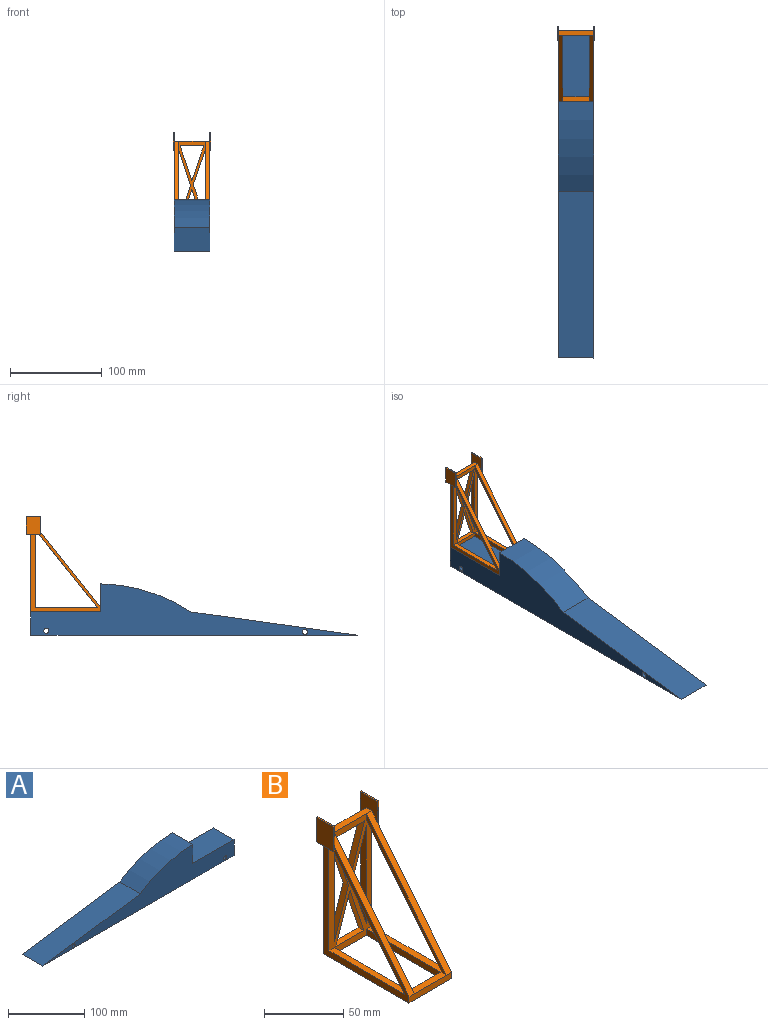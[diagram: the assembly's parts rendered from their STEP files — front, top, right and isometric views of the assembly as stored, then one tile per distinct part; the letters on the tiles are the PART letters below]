
ASSEMBLY  parts=2 mates=1
PART A: 10 faces, bbox 355.6x38.1x55.9 mm
  f0: plane 38.1x25.4mm, normal (1,0,0), area 967.7mm2, adj f1,f5,f6,f7
  f1: plane 76.2x38.1mm, normal (0,0,1), area 2903.2mm2, adj f0,f2,f6,f7
  f2: plane 38.1x30.48mm, normal (1,0,0), area 1161.3mm2, adj f1,f3,f6,f7
  f3: cylinder r=183.28mm len=97.84mm, axis (0,1,0), area 3957mm2, adj f2,f4,f6,f7
  f4: plane 181.56x38.1mm, normal (-0.14,0,0.99), area 6984.9mm2, adj f3,f5,f6,f7
  f5: plane 355.6x38.1mm, normal (0,0,-1), area 13548.4mm2, adj f0,f4,f6,f7
  f6: plane 355.6x55.88mm, normal (0,-1,0), area 8669.6mm2, adj f0,f1,f2,f3,f4,f5,f8,f9
  f7: plane 355.6x55.88mm, normal (0,1,0), area 8669.6mm2, adj f0,f1,f2,f3,f4,f5,f8,f9
  f8: cylinder r=2.79mm len=38.1mm, axis (0,-1,0), area 668.9mm2, adj f6,f7
  f9: cylinder r=2.79mm len=38.1mm, axis (0,-1,0), area 668.9mm2, adj f6,f7
PART B: 43 faces, bbox 40.6x81.4x103.5 mm
  f0: plane 66.68x4.76mm, normal (-1,0,0), area 317.5mm2, adj f3,f8,f20,f42
  f1: plane 66.68x4.76mm, normal (1,0,0), area 317.5mm2, adj f3,f8,f20,f42
  f2: plane 87.44x76.2mm, normal (-1,0,0), area 1049.8mm2, adj f3,f8,f11,f20,f22,f26,f27,f29
  f3: plane 93.98x38.1mm, normal (0,-1,0), area 1575.4mm2, adj f0,f1,f2,f4,f5,f6,f7,f8
  f4: plane 25.59x4.76mm, normal (0,0,-1), area 121.9mm2, adj f3,f11,f12,f13
  f5: plane 75.73x4.76mm, normal (-1,0,0), area 360.7mm2, adj f3,f11,f14,f15
  f6: plane 25.1x4.76mm, normal (0,0,1), area 119.6mm2, adj f3,f11,f16,f17
  f7: plane 75.32x4.76mm, normal (1,0,0), area 358.7mm2, adj f3,f11,f18,f19
  f8: plane 76.2x38.1mm, normal (0,0,-1), area 998mm2, adj f0,f1,f2,f3,f9,f11,f22,f42
  f9: plane 87.44x76.2mm, normal (1,0,0), area 1049.9mm2, adj f3,f8,f11,f20,f22,f24,f25,f37
  f10: plane 38.1x4.76mm, normal (0,0,1), area 181.5mm2, adj f3,f11,f24,f26,f34,f35
  f11: plane 93.98x38.1mm, normal (0,1,0), area 1666.1mm2, adj f2,f4,f5,f6,f7,f8,f9,f10
  f12: plane 37.82x12.8mm, normal (0.95,0,0.32), area 190.2mm2, adj f3,f4,f11,f13
  f13: plane 37.82x12.8mm, normal (-0.95,0,0.32), area 190.2mm2, adj f3,f4,f11,f12
  f14: plane 37.69x12.87mm, normal (0.95,0,-0.32), area 189.7mm2, adj f3,f5,f11,f15
  f15: plane 38.04x12.87mm, normal (0.95,0,0.32), area 191.3mm2, adj f3,f5,f11,f14
  f16: plane 37.38x12.34mm, normal (-0.95,0,-0.31), area 187.5mm2, adj f3,f6,f11,f17
  f17: plane 37.38x12.77mm, normal (0.95,0,-0.32), area 188.1mm2, adj f3,f6,f11,f16
  f18: plane 37.19x12.58mm, normal (-0.95,0,0.32), area 187mm2, adj f3,f7,f11,f19
  f19: plane 38.13x12.58mm, normal (-0.95,0,-0.31), area 191.2mm2, adj f3,f7,f11,f18
  f20: plane 71.44x38.1mm, normal (0,0,1), area 780.2mm2, adj f0,f1,f2,f3,f9,f21,f22,f23
  f21: plane 89.22x71.44mm, normal (-1,0,0), area 331.1mm2, adj f3,f20,f24,f25
  f22: plane 38.1x4.76mm, normal (0,-1,0), area 181.5mm2, adj f2,f8,f9,f20,f24,f26
  f23: plane 89.22x71.44mm, normal (1,0,0), area 331mm2, adj f3,f20,f26,f27
  f24: plane 89.22x71.44mm, normal (0,-0.78,0.63), area 544.3mm2, adj f9,f10,f21,f22,f35
  f25: plane 84.46x67.62mm, normal (0,0.78,-0.63), area 515.3mm2, adj f3,f9,f20,f21,f36
  f26: plane 89.22x71.44mm, normal (0,-0.78,0.63), area 544.3mm2, adj f2,f10,f22,f23,f34
  f27: plane 84.46x67.63mm, normal (0,0.78,-0.63), area 515.3mm2, adj f2,f3,f20,f23,f28
  f28: plane 4.76x3.81mm, normal (1,0,0), area 9.1mm2, adj f3,f27,f29
  f29: plane 15.24x1.27mm, normal (0,0,-1), area 19.4mm2, adj f2,f28,f30,f32,f33,f34
  f30: plane 19.05x1.27mm, normal (0,-1,0), area 24.2mm2, adj f2,f29,f31,f33,f34
  f31: plane 15.24x1.27mm, normal (0,0,1), area 19.4mm2, adj f30,f32,f33,f34
  f32: plane 19.05x1.27mm, normal (0,1,0), area 24.2mm2, adj f29,f31,f33,f34
  f33: plane 19.05x15.24mm, normal (-1,0,0), area 290.3mm2, adj f29,f30,f31,f32
  f34: plane 19.05x15.24mm, normal (1,0,0), area 212.2mm2, adj f10,f11,f26,f29,f30,f31,f32
  f35: plane 19.05x15.24mm, normal (-1,0,0), area 212.2mm2, adj f10,f11,f24,f37,f38,f39,f40
  f36: plane 4.76x3.81mm, normal (-1,0,0), area 9.1mm2, adj f3,f25,f38
  f37: plane 19.05x1.27mm, normal (0,-1,0), area 24.2mm2, adj f9,f35,f38,f40,f41
  f38: plane 15.24x1.27mm, normal (0,0,-1), area 19.4mm2, adj f9,f35,f36,f37,f39,f41
  f39: plane 19.05x1.27mm, normal (0,1,0), area 24.2mm2, adj f35,f38,f40,f41
  f40: plane 15.24x1.27mm, normal (0,0,1), area 19.4mm2, adj f35,f37,f39,f41
  f41: plane 19.05x15.24mm, normal (1,0,0), area 290.3mm2, adj f37,f38,f39,f40
  f42: plane 28.58x4.76mm, normal (0,1,0), area 136.1mm2, adj f0,f1,f8,f20
PLACE A rot(axis=(0,0,1),90deg) t=(229.47,-163.43,16.32)mm
PLACE B t=(248.52,87.94,88.71)mm
MATE fastened B.f8 <-> A.f1  axis (0,0,-1) through (248.52,52.22,41.72)mm
